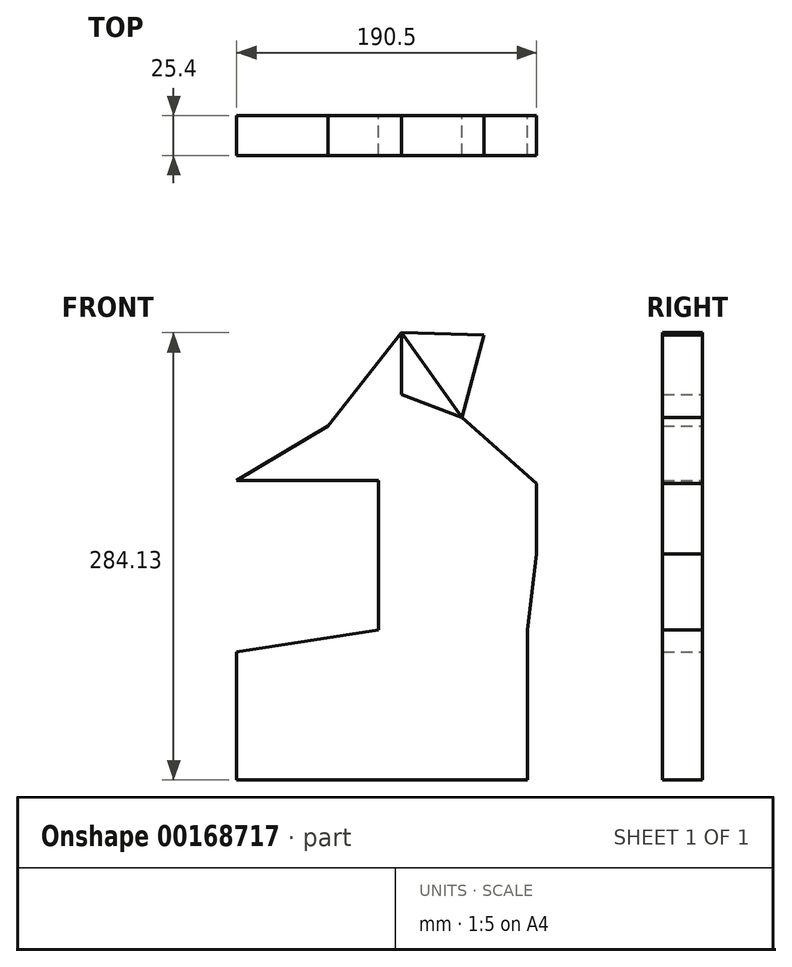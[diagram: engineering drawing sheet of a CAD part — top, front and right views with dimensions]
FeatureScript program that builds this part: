
annotation { "Feature Type Name" : "Feature", "Feature Type Description" : "" }
export const myFeature = defineFeature(function(context is Context, id is Id, definition is map)
    precondition{}
    {
        {
            var Q0;
            Q0=qCreatedBy(makeId("Front.planeOp"),FACE);
            var sketch = newSketch(context, id + "F0", { "sketchPlane" : qUnion([Q0])});
            skLineSegment(sketch, "E0", {"start": v(0, 0) * mm, "end": v(94.6, 0) * mm});
            skLineSegment(sketch, "E1", {"start": v(94.6, 0) * mm, "end": v(94.6, -95.2) * mm});
            skLineSegment(sketch, "E2", {"start": v(94.6, -95.2) * mm, "end": v(0, -95.2) * mm});
            skLineSegment(sketch, "E3", {"start": v(0, -95.2) * mm, "end": v(-89.95, -95.2) * mm});
            skLineSegment(sketch, "E4", {"start": v(-89.95, -95.2) * mm, "end": v(-89.95, -13.77) * mm});
            skLineSegment(sketch, "E5", {"start": v(-89.95, -13.77) * mm, "end": v(-89.95, 43.55) * mm});
            skLineSegment(sketch, "E6", {"start": v(-89.95, 43.55) * mm, "end": v(-89.95, 95.04) * mm});
            skLineSegment(sketch, "E7", {"start": v(-89.95, 95.04) * mm, "end": v(0, 95.04) * mm});
            skLineSegment(sketch, "E8", {"start": v(0, 95.04) * mm, "end": v(53.13, 95.04) * mm});
            skLineSegment(sketch, "E9", {"start": v(53.13, 95.04) * mm, "end": v(53.13, 95.04) * mm});
            skLineSegment(sketch, "E10", {"start": v(81.86, 93.22) * mm, "end": v(100.55, 93.22) * mm});
            skLineSegment(sketch, "E11", {"start": v(100.55, 93.22) * mm, "end": v(100.55, 48.5) * mm});
            skLineSegment(sketch, "E12", {"start": v(100.55, 48.5) * mm, "end": v(94.6, 0) * mm});
            skLineSegment(sketch, "E13", {"start": v(81.86, 93.22) * mm, "end": v(53.13, 95.04) * mm});
            skLineSegment(sketch, "E14", {"start": v(-89.95, -13.77) * mm, "end": v(0, 0) * mm});
            skLineSegment(sketch, "E15", {"start": v(0, 95.04) * mm, "end": v(0, 0) * mm});
            skLineSegment(sketch, "E16", {"start": v(0, 0) * mm, "end": v(0, -95.2) * mm});
            skLineSegment(sketch, "E17", {"start": v(-31.96, 129.72) * mm, "end": v(-31.96, 129.72) * mm});
            skLineSegment(sketch, "E18", {"start": v(-31.96, 129.72) * mm, "end": v(-89.95, 95.04) * mm});
            skLineSegment(sketch, "E19", {"start": v(-31.96, 129.72) * mm, "end": v(14.6, 188.94) * mm});
            skLineSegment(sketch, "E20", {"start": v(14.6, 188.94) * mm, "end": v(14.66, 149.74) * mm});
            skLineSegment(sketch, "E21", {"start": v(14.66, 149.74) * mm, "end": v(53, 135.12) * mm});
            skLineSegment(sketch, "E22", {"start": v(53, 135.12) * mm, "end": v(100.55, 93.22) * mm});
            skLineSegment(sketch, "E23", {"start": v(67.17, 187.35) * mm, "end": v(53, 135.12) * mm});
            skLineSegment(sketch, "E24", {"start": v(53, 135.12) * mm, "end": v(14.6, 188.94) * mm});
            skLineSegment(sketch, "E25", {"start": v(14.6, 188.94) * mm, "end": v(67.17, 187.35) * mm});
            skSolve(sketch);
        }
        {
            var Q0;
            Q0=makeQuery(id+"F0.imprint","IMPRINT",FACE,{"disambiguationData":[TD([[makeQuery(id+"F0.imprint","IMPRINT",EDGE,{"derivedFrom":sQuery(id+"F0.wireOp",EDGE,"E3")}),-1.0]])]});
            var Q1;
            Q1=makeQuery(id+"F0.imprint","IMPRINT",FACE,{"disambiguationData":[TD([[makeQuery(id+"F0.imprint","IMPRINT",EDGE,{"derivedFrom":sQuery(id+"F0.wireOp",EDGE,"E7")}),1.0]])]});
            var Q2;
            Q2=makeQuery(id+"F0.imprint","IMPRINT",FACE,{"disambiguationData":[TD([[makeQuery(id+"F0.imprint","IMPRINT",EDGE,{"derivedFrom":sQuery(id+"F0.wireOp",EDGE,"E23")}),-1.0]])]});
            var Q3;
            Q3=makeQuery(id+"F0.imprint","IMPRINT",FACE,{"disambiguationData":[TD([[makeQuery(id+"F0.imprint","IMPRINT",EDGE,{"derivedFrom":sQuery(id+"F0.wireOp",EDGE,"E0")}),-1.0]])]});
            var Q4;
            Q4=makeQuery(id+"F0.imprint","IMPRINT",FACE,{"disambiguationData":[TD([[makeQuery(id+"F0.imprint","IMPRINT",EDGE,{"derivedFrom":sQuery(id+"F0.wireOp",EDGE,"E0")}),1.0]])]});
            extrude(context, id + "F1", {"entities" : qUnion([Q0, Q1, Q2, Q3, Q4]), "depth" : 25.4 * mm});
        }
    });
